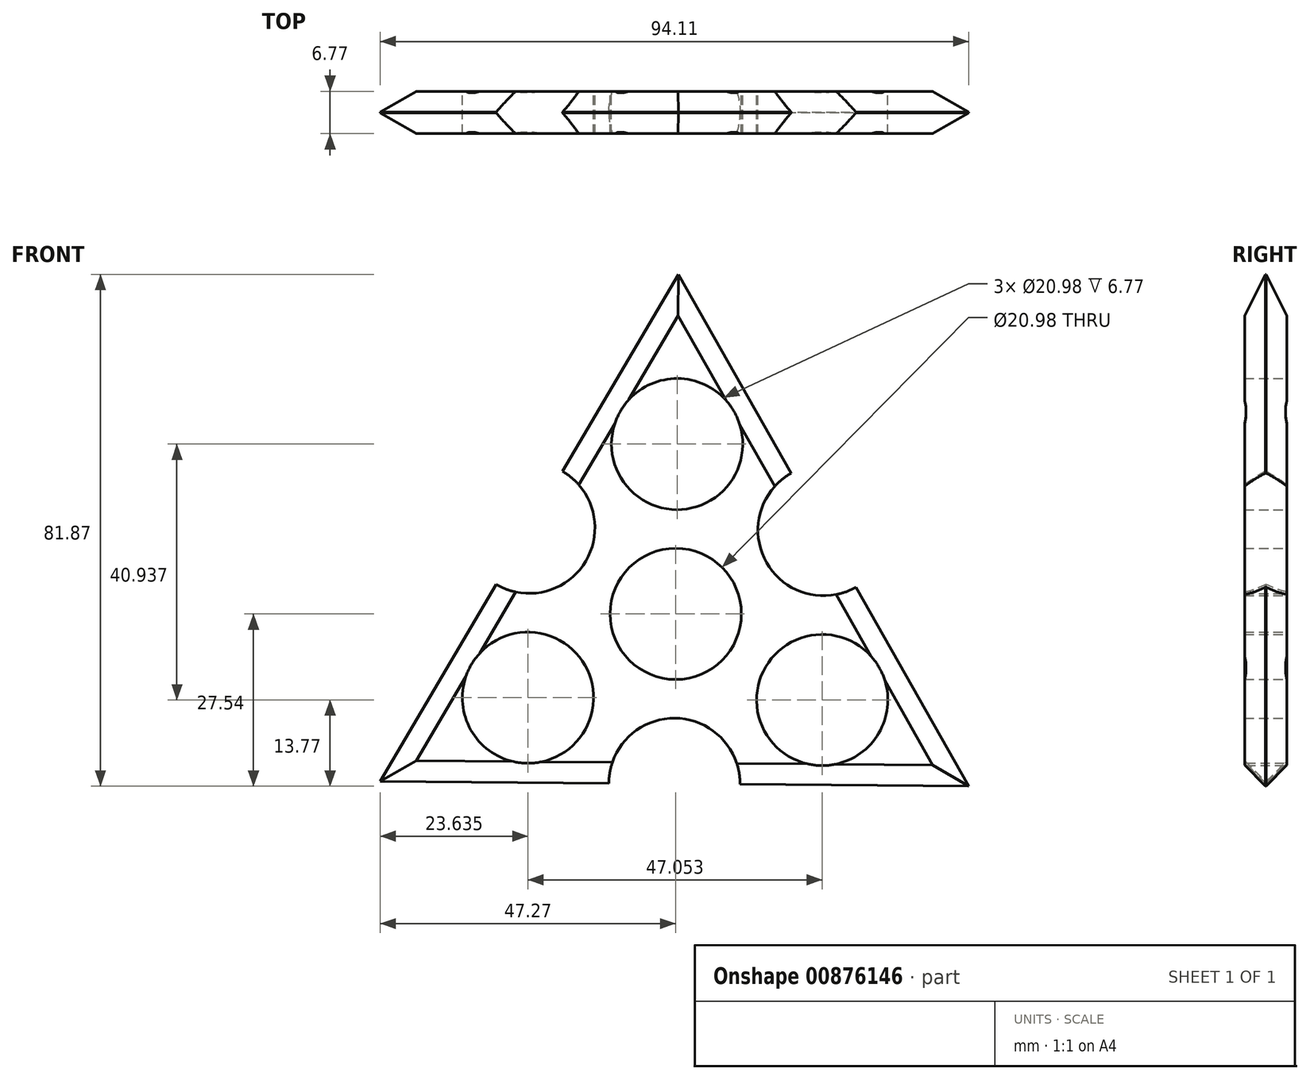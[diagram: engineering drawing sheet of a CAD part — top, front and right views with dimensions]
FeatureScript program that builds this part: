
annotation { "Feature Type Name" : "Feature", "Feature Type Description" : "" }
export const myFeature = defineFeature(function(context is Context, id is Id, definition is map)
    precondition{}
    {
        {
            var Q0;
            Q0=qCreatedBy(makeId("Front.planeOp"),FACE);
            var sketch = newSketch(context, id + "F0", { "sketchPlane" : qUnion([Q0])});
            skCircle(sketch, "E0.cCircle", {"center": v(0, 0) * mm, "radius": 27.17 * mm, "construction": true});
            skLineSegment(sketch, "E0.0", {"start": v(0.43, 54.33) * mm, "end": v(46.84, -27.54) * mm});
            skLineSegment(sketch, "E0.1", {"start": v(46.84, -27.54) * mm, "end": v(-47.27, -26.8) * mm});
            skLineSegment(sketch, "E0.2", {"start": v(-47.27, -26.8) * mm, "end": v(0.43, 54.33) * mm});
            skPoint(sketch, "E0.0.midPoint", {"position": v(23.63, 13.4) * mm});
            skCircle(sketch, "E1", {"center": v(0, 0) * mm, "radius": 10.5 * mm});
            skCircle(sketch, "E2", {"center": v(23.63, 13.4) * mm, "radius": 10.5 * mm});
            skCircle(sketch, "E3.1.0", {"center": v(-23.42, 13.77) * mm, "radius": 10.5 * mm});
            skCircle(sketch, "E3.2.0", {"center": v(-0.22, -27.17) * mm, "radius": 10.5 * mm});
            skLineSegment(sketch, "E3.anchor1", {"start": v(0, 0) * mm, "end": v(23.63, 13.4) * mm, "construction": true});
            skLineSegment(sketch, "E3.anchor2", {"start": v(0, 0) * mm, "end": v(-0.22, -27.17) * mm, "construction": true});
            skCircle(sketch, "E4.1.0", {"center": v(-23.63, -13.4) * mm, "radius": 10.5 * mm});
            skCircle(sketch, "E4.1.1", {"center": v(0.22, 27.17) * mm, "radius": 10.5 * mm});
            skCircle(sketch, "E4.1.2", {"center": v(23.42, -13.77) * mm, "radius": 10.5 * mm});
            skLineSegment(sketch, "E4.anchor2", {"start": v(0, 0) * mm, "end": v(-23.42, 13.77) * mm, "construction": true});
            skSolve(sketch);
        }
        {
            var Q0;
            Q0=makeQuery(id+"F0.imprint","IMPRINT",FACE,{"disambiguationData":[TD([[makeQuery(id+"F0.imprint","IMPRINT",EDGE,{"derivedFrom":sQuery(id+"F0.wireOp",EDGE,"E1")}),-1.0]])]});
            extrude(context, id + "F1", {"entities" : qUnion([Q0]), "depth" : 6.77 * mm, "offsetDistance" : 25 * mm});
        }
        {
            var Q0;
            {var subQ0=sQuery(id+"F0.wireOp",EDGE,"E0.2");Q0=makeQuery(id+"F1.opExtrude","CAP_EDGE",EDGE,{"disambiguationData":[OSD([subQ0]),TDD([makeQuery(id+"F0.imprint","IMPRINT",EDGE,{"disambiguationData":[TD([[makeQuery(id+"F0.imprint","INTERSECT",VERTEX,{"derivedFrom":[sQuery(id+"F0.wireOp",EDGE,"E0.1"),subQ0]}),-1.0]])],"derivedFrom":subQ0})])],"isStart":false});}
            var Q1;
            Q1=makeQuery(id+"F1.opExtrude","CAP_EDGE",EDGE,{"disambiguationData":[OSD([sQuery(id+"F0.wireOp",EDGE,"E3.1.0")])],"isStart":false});
            var Q2;
            {var subQ0=sQuery(id+"F0.wireOp",EDGE,"E0.2");Q2=makeQuery(id+"F1.opExtrude","CAP_EDGE",EDGE,{"disambiguationData":[OSD([subQ0]),TDD([makeQuery(id+"F0.imprint","IMPRINT",EDGE,{"disambiguationData":[TD([[makeQuery(id+"F0.imprint","INTERSECT",VERTEX,{"derivedFrom":[sQuery(id+"F0.wireOp",EDGE,"E0.0"),subQ0]}),1.0]])],"derivedFrom":subQ0})])],"isStart":false});}
            var Q3;
            {var subQ0=sQuery(id+"F0.wireOp",EDGE,"E0.0");Q3=makeQuery(id+"F1.opExtrude","CAP_EDGE",EDGE,{"disambiguationData":[OSD([subQ0]),TDD([makeQuery(id+"F0.imprint","IMPRINT",EDGE,{"disambiguationData":[TD([[makeQuery(id+"F0.imprint","INTERSECT",VERTEX,{"derivedFrom":[subQ0,sQuery(id+"F0.wireOp",EDGE,"E0.2")]}),-1.0]])],"derivedFrom":subQ0})])],"isStart":false});}
            var Q4;
            Q4=makeQuery(id+"F1.opExtrude","CAP_EDGE",EDGE,{"disambiguationData":[OSD([sQuery(id+"F0.wireOp",EDGE,"E2")])],"isStart":false});
            var Q5;
            {var subQ0=sQuery(id+"F0.wireOp",EDGE,"E0.1");Q5=makeQuery(id+"F1.opExtrude","CAP_EDGE",EDGE,{"disambiguationData":[OSD([subQ0]),TDD([makeQuery(id+"F0.imprint","IMPRINT",EDGE,{"disambiguationData":[TD([[makeQuery(id+"F0.imprint","INTERSECT",VERTEX,{"derivedFrom":[subQ0,sQuery(id+"F0.wireOp",EDGE,"E0.2")]}),1.0]])],"derivedFrom":subQ0})])],"isStart":false});}
            var Q6;
            Q6=makeQuery(id+"F1.opExtrude","CAP_EDGE",EDGE,{"disambiguationData":[OSD([sQuery(id+"F0.wireOp",EDGE,"E3.2.0")])],"isStart":false});
            var Q7;
            {var subQ0=sQuery(id+"F0.wireOp",EDGE,"E0.1");Q7=makeQuery(id+"F1.opExtrude","CAP_EDGE",EDGE,{"disambiguationData":[OSD([subQ0]),TDD([makeQuery(id+"F0.imprint","IMPRINT",EDGE,{"disambiguationData":[TD([[makeQuery(id+"F0.imprint","INTERSECT",VERTEX,{"derivedFrom":[sQuery(id+"F0.wireOp",EDGE,"E0.0"),subQ0]}),-1.0]])],"derivedFrom":subQ0})])],"isStart":false});}
            var Q8;
            {var subQ0=sQuery(id+"F0.wireOp",EDGE,"E0.0");Q8=makeQuery(id+"F1.opExtrude","CAP_EDGE",EDGE,{"disambiguationData":[OSD([subQ0]),TDD([makeQuery(id+"F0.imprint","IMPRINT",EDGE,{"disambiguationData":[TD([[makeQuery(id+"F0.imprint","INTERSECT",VERTEX,{"derivedFrom":[subQ0,sQuery(id+"F0.wireOp",EDGE,"E0.1")]}),1.0]])],"derivedFrom":subQ0})])],"isStart":false});}
            var Q9;
            {var subQ0=sQuery(id+"F0.wireOp",EDGE,"E0.0");Q9=makeQuery(id+"F1.opExtrude","CAP_EDGE",EDGE,{"disambiguationData":[OSD([subQ0]),TDD([makeQuery(id+"F0.imprint","IMPRINT",EDGE,{"disambiguationData":[TD([[makeQuery(id+"F0.imprint","INTERSECT",VERTEX,{"derivedFrom":[subQ0,sQuery(id+"F0.wireOp",EDGE,"E0.2")]}),-1.0]])],"derivedFrom":subQ0})])],"isStart":true});}
            var Q10;
            {var subQ0=sQuery(id+"F0.wireOp",EDGE,"E0.2");Q10=makeQuery(id+"F1.opExtrude","CAP_EDGE",EDGE,{"disambiguationData":[OSD([subQ0]),TDD([makeQuery(id+"F0.imprint","IMPRINT",EDGE,{"disambiguationData":[TD([[makeQuery(id+"F0.imprint","INTERSECT",VERTEX,{"derivedFrom":[sQuery(id+"F0.wireOp",EDGE,"E0.0"),subQ0]}),1.0]])],"derivedFrom":subQ0})])],"isStart":true});}
            var Q11;
            Q11=makeQuery(id+"F1.opExtrude","CAP_EDGE",EDGE,{"disambiguationData":[OSD([sQuery(id+"F0.wireOp",EDGE,"E3.1.0")])],"isStart":true});
            var Q12;
            {var subQ0=sQuery(id+"F0.wireOp",EDGE,"E0.2");Q12=makeQuery(id+"F1.opExtrude","CAP_EDGE",EDGE,{"disambiguationData":[OSD([subQ0]),TDD([makeQuery(id+"F0.imprint","IMPRINT",EDGE,{"disambiguationData":[TD([[makeQuery(id+"F0.imprint","INTERSECT",VERTEX,{"derivedFrom":[sQuery(id+"F0.wireOp",EDGE,"E0.1"),subQ0]}),-1.0]])],"derivedFrom":subQ0})])],"isStart":true});}
            var Q13;
            {var subQ0=sQuery(id+"F0.wireOp",EDGE,"E0.1");Q13=makeQuery(id+"F1.opExtrude","CAP_EDGE",EDGE,{"disambiguationData":[OSD([subQ0]),TDD([makeQuery(id+"F0.imprint","IMPRINT",EDGE,{"disambiguationData":[TD([[makeQuery(id+"F0.imprint","INTERSECT",VERTEX,{"derivedFrom":[subQ0,sQuery(id+"F0.wireOp",EDGE,"E0.2")]}),1.0]])],"derivedFrom":subQ0})])],"isStart":true});}
            var Q14;
            Q14=makeQuery(id+"F1.opExtrude","CAP_EDGE",EDGE,{"disambiguationData":[OSD([sQuery(id+"F0.wireOp",EDGE,"E3.2.0")])],"isStart":true});
            var Q15;
            {var subQ0=sQuery(id+"F0.wireOp",EDGE,"E0.1");Q15=makeQuery(id+"F1.opExtrude","CAP_EDGE",EDGE,{"disambiguationData":[OSD([subQ0]),TDD([makeQuery(id+"F0.imprint","IMPRINT",EDGE,{"disambiguationData":[TD([[makeQuery(id+"F0.imprint","INTERSECT",VERTEX,{"derivedFrom":[sQuery(id+"F0.wireOp",EDGE,"E0.0"),subQ0]}),-1.0]])],"derivedFrom":subQ0})])],"isStart":true});}
            var Q16;
            {var subQ0=sQuery(id+"F0.wireOp",EDGE,"E0.0");Q16=makeQuery(id+"F1.opExtrude","CAP_EDGE",EDGE,{"disambiguationData":[OSD([subQ0]),TDD([makeQuery(id+"F0.imprint","IMPRINT",EDGE,{"disambiguationData":[TD([[makeQuery(id+"F0.imprint","INTERSECT",VERTEX,{"derivedFrom":[subQ0,sQuery(id+"F0.wireOp",EDGE,"E0.1")]}),1.0]])],"derivedFrom":subQ0})])],"isStart":true});}
            var Q17;
            Q17=makeQuery(id+"F1.opExtrude","CAP_EDGE",EDGE,{"disambiguationData":[OSD([sQuery(id+"F0.wireOp",EDGE,"E2")])],"isStart":true});
            chamfer(context, id + "F2", {"entities" : qUnion([Q0, Q1, Q2, Q3, Q4, Q5, Q6, Q7, Q8, Q9, Q10, Q11, Q12, Q13, Q14, Q15, Q16, Q17]), "width" : 3.33 * mm, "tangentPropagation" : true});
        }
    });
